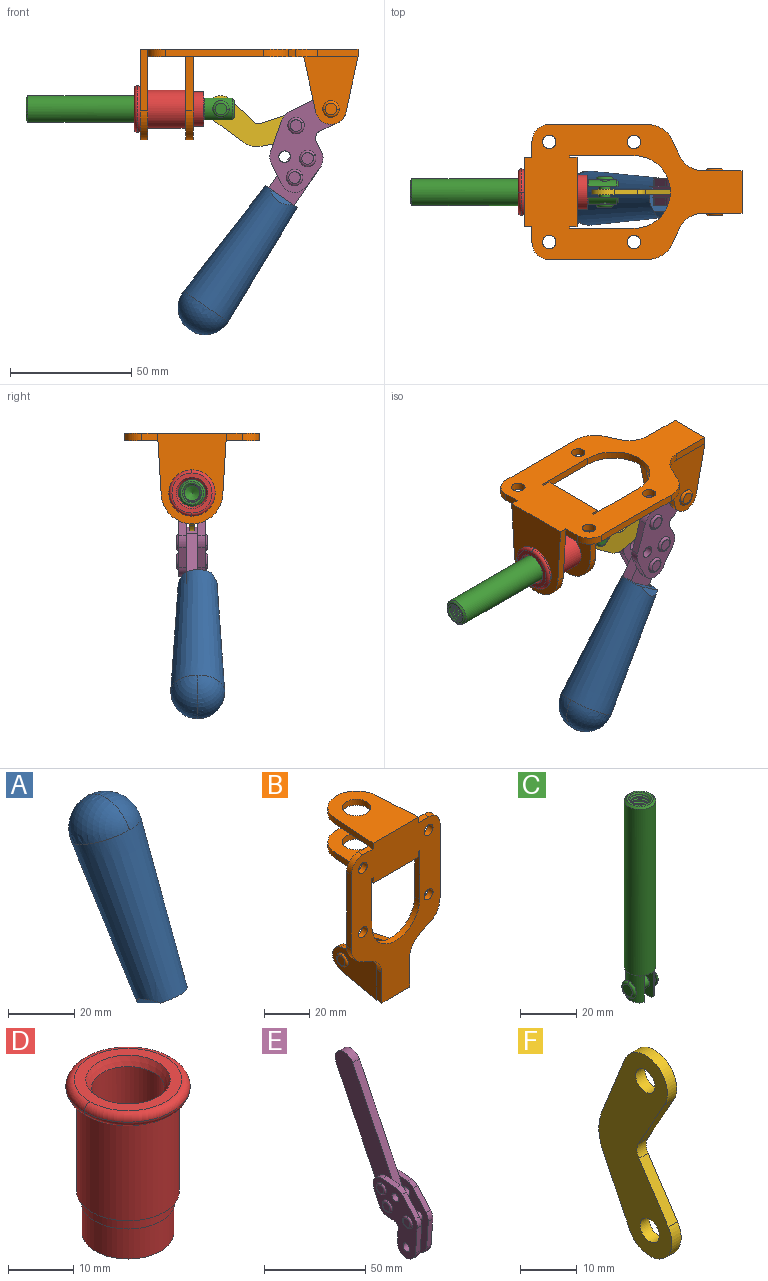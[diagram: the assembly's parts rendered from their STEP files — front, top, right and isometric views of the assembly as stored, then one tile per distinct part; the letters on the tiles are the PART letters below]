
ASSEMBLY  parts=6 mates=6
PART A: 11 faces, bbox 22.3x42.6x64.5 mm
  f0: sphere r=11.13mm, area 411.4mm2, adj f1,f8
  f1: cone r=11.11mm half-angle=3.3deg, axis (0,0.44,0.9), area 3251.8mm2, adj f0,f7,f8,f9,f10
  f2: cylinder r=6.16mm len=11.7mm, axis (1,0,0), area 89.5mm2, adj f3,f4,f5,f6
  f3: plane 60.23x36.75mm, normal (-1,0,0), area 763.6mm2, adj f2,f4,f6,f10
  f4: plane 51.37x25.05mm, normal (0,0.9,-0.44), area 264.2mm2, adj f2,f3,f5,f10
  f5: plane 60.23x36.75mm, normal (1,0,0), area 763.6mm2, adj f2,f4,f6,f10
  f6: plane 51.37x25.05mm, normal (0,-0.9,0.44), area 264.2mm2, adj f2,f3,f5,f10
  f7: plane 9.95x5.95mm, normal (0.71,-0.31,-0.64), area 25.8mm2, adj f1,f10
  f8: sphere r=11.13mm, area 411.4mm2, adj f0,f1
  f9: plane 9.95x5.95mm, normal (-0.71,-0.31,-0.64), area 25.8mm2, adj f1,f10
  f10: plane 14.27x11.38mm, normal (0,-0.44,-0.9), area 106.7mm2, adj f1,f3,f4,f5,f6,f7,f9
PART B: 55 faces, bbox 55.7x37.4x89.8 mm
  f0: torus R=2.41mm, axis (-1,0,0), area 15mm2, adj f11,f15,f25
  f1: torus R=2.41mm, axis (-1,0,0), area 15mm2, adj f10,f12,f22
  f2: cylinder r=2.78mm len=5.56mm, axis (0,-1,0), area 54.2mm2, adj f30,f54
  f3: cylinder r=14.99mm len=29.97mm, axis (0,-1,0), area 145.9mm2, adj f30,f49,f53,f54
  f4: cylinder r=2.78mm len=5.56mm, axis (0,-1,0), area 54.2mm2, adj f30,f54
  f5: cylinder r=2.78mm len=5.56mm, axis (0,-1,0), area 54.2mm2, adj f30,f54
  f6: cylinder r=2.78mm len=5.56mm, axis (0,-1,0), area 54.2mm2, adj f30,f54
  f7: cylinder r=6.35mm len=12.7mm, axis (0,0,1), area 123.6mm2, adj f27,f51
  f8: cylinder r=6.35mm len=12.7mm, axis (0,0,-1), area 124.7mm2, adj f21,f35
  f9: cylinder r=2.41mm len=11.18mm, axis (-1,0,0), area 169.4mm2, adj f16,f19
  f10: plane 4.83x4.83mm, normal (1,0,0), area 18.3mm2, adj f1,f12
  f11: plane 4.83x4.83mm, normal (-1,0,0), area 18.3mm2, adj f0,f15
  f12: torus R=2.41mm, axis (-1,0,0), area 15mm2, adj f1,f10,f22
  f13: cylinder r=6.35mm len=12.41mm, axis (1,0,0), area 53.4mm2, adj f18,f19,f22,f23
  f14: cylinder r=6.35mm len=12.41mm, axis (-1,0,0), area 53.4mm2, adj f16,f17,f24,f25
  f15: torus R=2.41mm, axis (-1,0,0), area 15mm2, adj f0,f11,f25
  f16: plane 27.86x22.35mm, normal (1,0,0), area 425.4mm2, adj f9,f14,f17,f24,f30
  f17: plane 22.86x4.97mm, normal (0,0.21,0.98), area 72.5mm2, adj f14,f16,f25,f30
  f18: plane 22.86x4.97mm, normal (0,0.21,0.98), area 72.5mm2, adj f13,f19,f22,f30
  f19: plane 27.86x22.35mm, normal (-1,0,0), area 425.4mm2, adj f9,f13,f18,f23,f30
  f20: cylinder r=12.7mm len=25.35mm, axis (0,0,-1), area 119.8mm2, adj f21,f34,f35,f36
  f21: plane 34.21x28.07mm, normal (0,0,-1), area 702.4mm2, adj f8,f20,f30,f34,f36
  f22: plane 27.96x22.45mm, normal (1,0,0), area 407.2mm2, adj f1,f12,f13,f18,f23,f30,f42,f43
  f23: plane 22.86x4.97mm, normal (0,0.21,-0.98), area 72.5mm2, adj f13,f19,f22,f44
  f24: plane 22.86x4.97mm, normal (0,0.21,-0.98), area 72.5mm2, adj f14,f16,f25,f44
  f25: plane 27.86x22.35mm, normal (-1,0,0), area 407.1mm2, adj f0,f14,f15,f17,f24,f30,f45,f46
  f26: plane 3.1x0.95mm, normal (0,0,-1), area 2.7mm2, adj f30,f49,f50,f54
  f27: plane 34.21x28.07mm, normal (0,0,1), area 702.4mm2, adj f7,f28,f30,f50,f52
  f28: cylinder r=12.7mm len=25.35mm, axis (0,0,1), area 118.8mm2, adj f27,f50,f51,f52
  f29: plane 3.1x0.95mm, normal (0,0,-1), area 2.7mm2, adj f30,f52,f53,f54
  f30: plane 86.54x55.63mm, normal (0,1,0), area 2362.9mm2, adj f2,f3,f4,f5,f6,f16,f17,f18
  f31: plane 40.56x3.1mm, normal (-1,0,0), area 125.7mm2, adj f30,f32,f48,f54
  f32: cylinder r=7.11mm len=7.11mm, axis (0,-1,0), area 34.6mm2, adj f30,f31,f33,f54
  f33: plane 6.67x3.1mm, normal (0,0,1), area 20.4mm2, adj f30,f32,f34,f54
  f34: plane 25.39x3.13mm, normal (-1,0.06,0), area 79.5mm2, adj f20,f21,f33,f35,f54
  f35: plane 37.31x28.45mm, normal (0,0,1), area 789.9mm2, adj f8,f20,f34,f36,f54
  f36: plane 25.39x3.13mm, normal (1,0.06,0), area 79.5mm2, adj f20,f21,f35,f37,f54
  f37: plane 6.67x3.1mm, normal (0,0,1), area 20.4mm2, adj f30,f36,f38,f54
  f38: cylinder r=7.11mm len=7.11mm, axis (0,-1,0), area 34.6mm2, adj f30,f37,f39,f54
  f39: plane 40.56x3.1mm, normal (1,0,0), area 125.7mm2, adj f30,f38,f40,f54
  f40: cylinder r=11.18mm len=10.16mm, axis (0,-1,0), area 39.5mm2, adj f30,f39,f41,f54
  f41: plane 6.09x3.1mm, normal (0.42,0,-0.91), area 20.8mm2, adj f30,f40,f42,f54
  f42: cylinder r=11.18mm len=9.41mm, axis (0,-1,0), area 37.2mm2, adj f22,f30,f41,f43,f54
  f43: plane 16.5x3.1mm, normal (1,0,0), area 51.1mm2, adj f22,f42,f44,f54
  f44: plane 17.37x3.1mm, normal (0,0,-1), area 53.8mm2, adj f23,f24,f30,f43,f45,f54
  f45: plane 16.5x3.1mm, normal (-1,0,0), area 51.1mm2, adj f25,f44,f46,f54
  f46: cylinder r=11.18mm len=9.41mm, axis (0,-1,0), area 37.2mm2, adj f25,f30,f45,f47,f54
  f47: plane 6.09x3.1mm, normal (-0.42,0,-0.91), area 20.8mm2, adj f30,f46,f48,f54
  f48: cylinder r=11.18mm len=10.16mm, axis (0,-1,0), area 39.5mm2, adj f30,f31,f47,f54
  f49: plane 26.54x3.1mm, normal (-1,0,0), area 82.3mm2, adj f3,f26,f30,f54
  f50: plane 25.39x3.1mm, normal (1,0.06,0), area 78.8mm2, adj f26,f27,f28,f51,f54
  f51: plane 37.31x28.45mm, normal (0,0,-1), area 789.9mm2, adj f7,f28,f50,f52,f54
  f52: plane 25.39x3.1mm, normal (-1,0.06,0), area 78.8mm2, adj f27,f28,f29,f51,f54
  f53: plane 26.54x3.1mm, normal (1,0,0), area 82.3mm2, adj f3,f29,f30,f54
  f54: plane 89.66x55.63mm, normal (0,-1,0), area 2678.5mm2, adj f2,f3,f4,f5,f6,f26,f29,f31
PART C: 48 faces, bbox 12.6x11.1x86.1 mm
  f0: torus R=2.41mm, axis (-1,0,0), area 15mm2, adj f30,f32,f34
  f1: torus R=2.41mm, axis (-1,0,0), area 15mm2, adj f29,f31,f33
  f2: cylinder r=5.54mm len=72.39mm, axis (0,0,1), area 2518.5mm2, adj f3,f4,f42,f43
  f3: cone r=5.54mm half-angle=45deg, axis (0,0,1), area 7.6mm2, adj f2,f5,f41
  f4: cone r=5.54mm half-angle=45deg, axis (0,0,-1), area 34.9mm2, adj f2,f39
  f5: cylinder r=5.08mm len=11.48mm, axis (0,0,1), area 108.3mm2, adj f3,f7,f8,f41
  f6: cylinder r=2.41mm len=4.83mm, axis (-1,0,0), area 71.2mm2, adj f40,f41
  f7: cylinder r=2.41mm len=4.83mm, axis (-1,0,0), area 7.6mm2, adj f5,f34
  f8: cone r=5.08mm half-angle=45deg, axis (0,0,1), area 10.6mm2, adj f5,f37,f41
  f9: cone r=3.98mm half-angle=45deg, axis (0,0,1), area 17.6mm2, adj f27,f39,f45,f46,f47
  f10: cylinder r=2.41mm len=4.83mm, axis (-1,0,0), area 7.6mm2, adj f33,f38
  f11: cylinder r=3.2mm len=6.4mm, axis (0,0,1), area 78.4mm2, adj f12,f28,f44,f45,f47
  f12: cylinder r=3.2mm len=6.4mm, axis (0,0,1), area 10.5mm2, adj f11,f13,f45,f47
  f13: cylinder r=3.2mm len=6.4mm, axis (0,0,1), area 10.5mm2, adj f12,f14,f45,f47
  f14: cylinder r=3.2mm len=6.4mm, axis (0,0,1), area 10.5mm2, adj f13,f15,f45,f47
  f15: cylinder r=3.2mm len=6.4mm, axis (0,0,1), area 10.5mm2, adj f14,f16,f45,f47
  f16: cylinder r=3.2mm len=6.4mm, axis (0,0,1), area 10.5mm2, adj f15,f17,f45,f47
  f17: cylinder r=3.2mm len=6.4mm, axis (0,0,1), area 10.5mm2, adj f16,f18,f45,f47
  f18: cylinder r=3.2mm len=6.4mm, axis (0,0,1), area 10.5mm2, adj f17,f19,f45,f47
  f19: cylinder r=3.2mm len=6.4mm, axis (0,0,1), area 10.5mm2, adj f18,f20,f45,f47
  f20: cylinder r=3.2mm len=6.4mm, axis (0,0,1), area 10.5mm2, adj f19,f21,f45,f47
  f21: cylinder r=3.2mm len=6.4mm, axis (0,0,1), area 10.5mm2, adj f20,f22,f45,f47
  f22: cylinder r=3.2mm len=6.4mm, axis (0,0,1), area 10.5mm2, adj f21,f23,f45,f47
  f23: cylinder r=3.2mm len=6.4mm, axis (0,0,1), area 10.5mm2, adj f22,f24,f45,f47
  f24: cylinder r=3.2mm len=6.4mm, axis (0,0,1), area 10.5mm2, adj f23,f25,f45,f47
  f25: cylinder r=3.2mm len=6.4mm, axis (0,0,1), area 10.5mm2, adj f24,f26,f45,f47
  f26: cylinder r=3.2mm len=6.4mm, axis (0,0,1), area 10.5mm2, adj f25,f27,f45,f47
  f27: cylinder r=3.2mm len=6.4mm, axis (0,0,1), area 7.4mm2, adj f9,f26,f45,f47
  f28: cone r=3.2mm half-angle=60deg, axis (0,0,1), area 37.2mm2, adj f11
  f29: plane 4.83x4.83mm, normal (-1,0,0), area 18.3mm2, adj f1,f31
  f30: plane 4.83x4.83mm, normal (1,0,0), area 18.3mm2, adj f0,f32
  f31: torus R=2.41mm, axis (-1,0,0), area 15mm2, adj f1,f29,f33
  f32: torus R=2.41mm, axis (-1,0,0), area 15mm2, adj f0,f30,f34
  f33: plane 6.83x6.83mm, normal (1,0,0), area 18.3mm2, adj f1,f10,f31
  f34: plane 6.83x6.83mm, normal (-1,0,0), area 18.3mm2, adj f0,f7,f32
  f35: cone r=5.08mm half-angle=45deg, axis (0,0,1), area 10.6mm2, adj f36,f38,f40
  f36: plane 7.25x1.97mm, normal (0,0,-1), area 10mm2, adj f35,f40
  f37: plane 7.25x1.97mm, normal (0,0,-1), area 10mm2, adj f8,f41
  f38: cylinder r=5.08mm len=11.48mm, axis (0,0,1), area 108.3mm2, adj f10,f35,f40,f42
  f39: plane 9.55x9.55mm, normal (0,0,1), area 22mm2, adj f4,f9
  f40: plane 12.76x10.09mm, normal (1,0,0), area 95.7mm2, adj f6,f35,f36,f38,f42,f43
  f41: plane 12.76x10.09mm, normal (-1,0,0), area 95.7mm2, adj f3,f5,f6,f8,f37,f43
  f42: cone r=5.54mm half-angle=45deg, axis (0,0,1), area 7.6mm2, adj f2,f38,f40
  f43: plane 11.07x4.7mm, normal (0,0,-1), area 50.4mm2, adj f2,f40,f41
  f44: plane 0.89x0.62mm, normal (-1,0,0), area 0.3mm2, adj f11,f45,f46,f47
  f45: bspline ~24.8x7.63mm, area 266.6mm2, adj f9,f11,f12,f13,f14,f15,f16,f17
  f46: bspline ~24.87x7.63mm, area 73.6mm2, adj f9,f44,f45,f47
  f47: bspline ~24.98x7.63mm, area 272.5mm2, adj f9,f11,f12,f13,f14,f15,f16,f17
PART D: 15 faces, bbox 20.6x20.6x28.7 mm
  f0: torus R=8.26mm, axis (0,0,1), area 56.8mm2, adj f1,f10,f12
  f1: torus R=8.26mm, axis (0,0,1), area 56.8mm2, adj f0,f6,f13
  f2: cylinder r=5.59mm len=25.91mm, axis (0,0,1), area 909.6mm2, adj f3,f4
  f3: cone r=6.86mm half-angle=45deg, axis (0,0,-1), area 70.2mm2, adj f2,f14
  f4: cone r=6.47mm half-angle=30deg, axis (0,0,1), area 66.7mm2, adj f2,f13
  f5: cylinder r=7.04mm len=14.07mm, axis (0,0,1), area 252.6mm2, adj f11,f14
  f6: torus R=8.26mm, axis (0,0,1), area 56.8mm2, adj f1,f12,f13
  f7: cylinder r=7.16mm len=14.33mm, axis (0,0,1), area 91.5mm2, adj f9,f11
  f8: cylinder r=7.86mm len=18.42mm, axis (0,0,1), area 909.6mm2, adj f9,f10
  f9: plane 15.72x15.72mm, normal (0,0,-1), area 33mm2, adj f7,f8
  f10: plane 16.51x16.51mm, normal (0,0,-1), area 19.9mm2, adj f0,f8,f12
  f11: plane 14.33x14.33mm, normal (0,0,-1), area 5.7mm2, adj f5,f7
  f12: torus R=8.26mm, axis (0,0,1), area 56.8mm2, adj f0,f6,f10
  f13: plane 16.51x16.51mm, normal (0,0,1), area 82.7mm2, adj f1,f4,f6
  f14: plane 14.07x14.07mm, normal (0,0,-1), area 7.8mm2, adj f3,f5
PART E: 59 faces, bbox 12.9x60.2x99.6 mm
  f0: torus R=2.39mm, axis (-1,0,0), area 14.9mm2, adj f20,f43,f51
  f1: torus R=2.39mm, axis (-1,0,0), area 14.9mm2, adj f19,f42,f51
  f2: torus R=2.39mm, axis (-1,0,0), area 14.9mm2, adj f18,f35,f51
  f3: torus R=2.39mm, axis (-1,0,0), area 14.9mm2, adj f14,f17,f23
  f4: torus R=2.39mm, axis (-1,0,0), area 14.9mm2, adj f13,f16,f23
  f5: torus R=2.39mm, axis (-1,0,0), area 14.9mm2, adj f12,f15,f23
  f6: cylinder r=2.39mm len=4.78mm, axis (1,0,0), area 46.5mm2, adj f48,f50,f51
  f7: cylinder r=2.39mm len=4.78mm, axis (1,0,0), area 46.5mm2, adj f50,f51
  f8: cylinder r=6.35mm len=12.68mm, axis (1,0,0), area 61.8mm2, adj f38,f39,f50,f51
  f9: cylinder r=2.39mm len=4.78mm, axis (-1,0,0), area 70.5mm2, adj f46,f50
  f10: cylinder r=2.39mm len=4.78mm, axis (-1,0,0), area 46.5mm2, adj f23,f45,f46
  f11: cylinder r=2.39mm len=4.78mm, axis (-1,0,0), area 46.5mm2, adj f23,f46
  f12: plane 4.78x4.78mm, normal (1,0,0), area 17.9mm2, adj f5,f15
  f13: plane 4.78x4.78mm, normal (1,0,0), area 17.9mm2, adj f4,f16
  f14: plane 4.78x4.78mm, normal (1,0,0), area 17.9mm2, adj f3,f17
  f15: torus R=2.39mm, axis (-1,0,0), area 14.9mm2, adj f5,f12,f23
  f16: torus R=2.39mm, axis (-1,0,0), area 14.9mm2, adj f4,f13,f23
  f17: torus R=2.39mm, axis (-1,0,0), area 14.9mm2, adj f3,f14,f23
  f18: plane 4.78x4.78mm, normal (-1,0,0), area 17.9mm2, adj f2,f35
  f19: plane 4.78x4.78mm, normal (-1,0,0), area 17.9mm2, adj f1,f42
  f20: plane 4.78x4.78mm, normal (-1,0,0), area 17.9mm2, adj f0,f43
  f21: plane 2.26x0.2mm, normal (1,0,0), area 0.2mm2, adj f31,f44
  f22: plane 2.26x0.2mm, normal (-1,0,0), area 0.2mm2, adj f41,f44
  f23: plane 39.37x30.77mm, normal (1,0,0), area 565.5mm2, adj f3,f4,f5,f10,f11,f15,f16,f17
  f24: cylinder r=6.1mm len=4.15mm, axis (-1,0,0), area 14.7mm2, adj f23,f25,f32,f46
  f25: plane 10.25x9.01mm, normal (0,-0.75,0.66), area 42.3mm2, adj f23,f24,f26,f46
  f26: cylinder r=6.35mm len=4.64mm, axis (-1,0,0), area 15.6mm2, adj f23,f25,f27,f46
  f27: plane 15.84x3.1mm, normal (0,-1,-0.07), area 49.2mm2, adj f23,f26,f28,f46
  f28: cylinder r=6.35mm len=12.68mm, axis (-1,0,0), area 61.8mm2, adj f23,f27,f29,f46
  f29: plane 8.11x3.1mm, normal (0,1,0.07), area 25.2mm2, adj f23,f28,f30,f46
  f30: cylinder r=3.05mm len=3.25mm, axis (-1,0,0), area 14.8mm2, adj f23,f29,f31,f46
  f31: plane 5.99x3.1mm, normal (0,0.07,-1), area 18.6mm2, adj f21,f23,f30,f44,f46
  f32: plane 9.5x3.1mm, normal (0,-0.07,1), area 29.5mm2, adj f23,f24,f33,f46,f47
  f33: cylinder r=6.1mm len=8.63mm, axis (-1,0,0), area 39.1mm2, adj f23,f32,f34,f47
  f34: plane 8.65x3.96mm, normal (0,0.91,-0.42), area 29.5mm2, adj f23,f33,f44,f47
  f35: torus R=2.39mm, axis (-1,0,0), area 14.9mm2, adj f2,f18,f51
  f36: plane 10.25x9.01mm, normal (0,-0.75,0.66), area 42.3mm2, adj f37,f49,f50,f51
  f37: cylinder r=6.35mm len=4.64mm, axis (1,0,0), area 15.6mm2, adj f36,f38,f50,f51
  f38: plane 15.84x3.1mm, normal (0,-1,-0.07), area 49.2mm2, adj f8,f37,f50,f51
  f39: plane 8.11x3.1mm, normal (0,1,0.07), area 25.2mm2, adj f8,f40,f50,f51
  f40: cylinder r=3.05mm len=3.25mm, axis (1,0,0), area 14.8mm2, adj f39,f41,f50,f51
  f41: plane 5.99x3.1mm, normal (0,0.07,-1), area 18.6mm2, adj f22,f40,f44,f50,f51
  f42: torus R=2.39mm, axis (-1,0,0), area 14.9mm2, adj f1,f19,f51
  f43: torus R=2.39mm, axis (-1,0,0), area 14.9mm2, adj f0,f20,f51
  f44: cylinder r=6.35mm len=12.12mm, axis (-1,0,0), area 128.9mm2, adj f21,f22,f23,f31,f34,f41,f46,f47
  f45: plane 2.65x1.35mm, normal (1,0,0), area 1mm2, adj f10,f55
  f46: plane 39.08x20.42mm, normal (-1,0,0), area 412.5mm2, adj f9,f10,f11,f24,f25,f26,f27,f28
  f47: plane 77.62x39.82mm, normal (1,0,0), area 850mm2, adj f32,f33,f34,f44,f53,f54,f55
  f48: plane 2.65x1.35mm, normal (-1,0,0), area 1mm2, adj f6,f55
  f49: cylinder r=6.1mm len=4.15mm, axis (1,0,0), area 14.7mm2, adj f36,f50,f51,f56
  f50: plane 39.08x20.42mm, normal (1,0,0), area 412.5mm2, adj f6,f7,f8,f9,f36,f37,f38,f39
  f51: plane 39.37x30.77mm, normal (-1,0,0), area 565.5mm2, adj f0,f1,f2,f6,f7,f8,f35,f36
  f52: plane 8.65x3.96mm, normal (0,0.91,-0.42), area 29.5mm2, adj f44,f51,f57,f58
  f53: plane 68.49x33.4mm, normal (0,0.9,-0.44), area 358.1mm2, adj f44,f47,f54,f58
  f54: cylinder r=6.35mm len=12.06mm, axis (1,0,0), area 93.7mm2, adj f47,f53,f55,f58
  f55: plane 68.49x33.4mm, normal (0,-0.9,0.44), area 358.1mm2, adj f44,f45,f46,f47,f48,f50,f54,f58
  f56: plane 9.5x3.1mm, normal (0,-0.07,1), area 29.5mm2, adj f49,f50,f51,f57,f58
  f57: cylinder r=6.1mm len=8.63mm, axis (1,0,0), area 39.1mm2, adj f51,f52,f56,f58
  f58: plane 77.62x39.82mm, normal (-1,0,0), area 850mm2, adj f44,f52,f53,f54,f55,f56,f57
PART F: 12 faces, bbox 2.3x18.2x42.8 mm
  f0: cylinder r=2.4mm len=4.8mm, axis (1,0,0), area 34.9mm2, adj f4,f11
  f1: cylinder r=10.41mm len=8.47mm, axis (1,0,0), area 20.2mm2, adj f4,f9,f10,f11
  f2: cylinder r=3.05mm len=3.16mm, axis (1,0,0), area 7.7mm2, adj f4,f6,f7,f11
  f3: cylinder r=2.4mm len=4.8mm, axis (1,0,0), area 34.9mm2, adj f4,f11
  f4: plane 42.81x18.23mm, normal (-1,0,0), area 414.1mm2, adj f0,f1,f2,f3,f5,f6,f7,f8
  f5: cylinder r=5.54mm len=10.67mm, axis (1,0,0), area 41.8mm2, adj f4,f6,f10,f11
  f6: plane 11.66x6.53mm, normal (0,-0.87,-0.49), area 30.9mm2, adj f2,f4,f5,f11
  f7: plane 11.17x7.33mm, normal (0,-0.84,0.55), area 30.9mm2, adj f2,f4,f8,f11
  f8: cylinder r=5.54mm len=10.51mm, axis (1,0,0), area 41.8mm2, adj f4,f7,f9,f11
  f9: plane 13.67x6.67mm, normal (0,0.9,-0.44), area 35.1mm2, adj f1,f4,f8,f11
  f10: plane 14.1x5.7mm, normal (0,0.93,0.37), area 35.1mm2, adj f1,f4,f5,f11
  f11: plane 42.81x18.23mm, normal (1,0,0), area 414.1mm2, adj f0,f1,f2,f3,f5,f6,f7,f8
PLACE A rot(axis=(0.71,-0.71,-0.05),174deg) t=(55.86,2.39,-65.67)mm
PLACE B rot(axis=(-0.58,-0.58,0.58),120deg) t=(-1.85,4.73,-1.55)mm fixed
PLACE C rot(axis=(-0.58,-0.58,0.58),120deg) t=(0.38,4.73,-1.55)mm
PLACE D rot(axis=(0.71,0,-0.71),180deg) t=(-1.85,29.35,-26.16)mm
PLACE E rot(axis=(-0.65,-0.65,0.38),138.3deg) t=(-9.81,4.73,-20.54)mm
PLACE F rot(axis=(-0.61,0.61,-0.51),126.2deg) t=(5.15,4.73,-5.99)mm
MATE cylindrical C.f2 <-> B.f7  axis (-1,0,0) through (-58.4,4.73,-26.16)mm
MATE revolute F.f3 <-> C.f6  axis (0,-1,0) through (-15.09,4.73,-26.16)mm
MATE fastened A.f2 <-> E.f54  axis (0,-1,0) through (-22.49,2.39,-109.35)mm
MATE revolute F.f5 <-> E.f4  axis (0,-1,0) through (15.92,4.73,-32.99)mm
MATE fastened D.f0 <-> B.f7  axis (1,0,0) through (-48.24,4.73,-26.16)mm
MATE revolute B.f0 <-> E.f7  axis (0,-1,0) through (30.24,4.73,-26.16)mm
